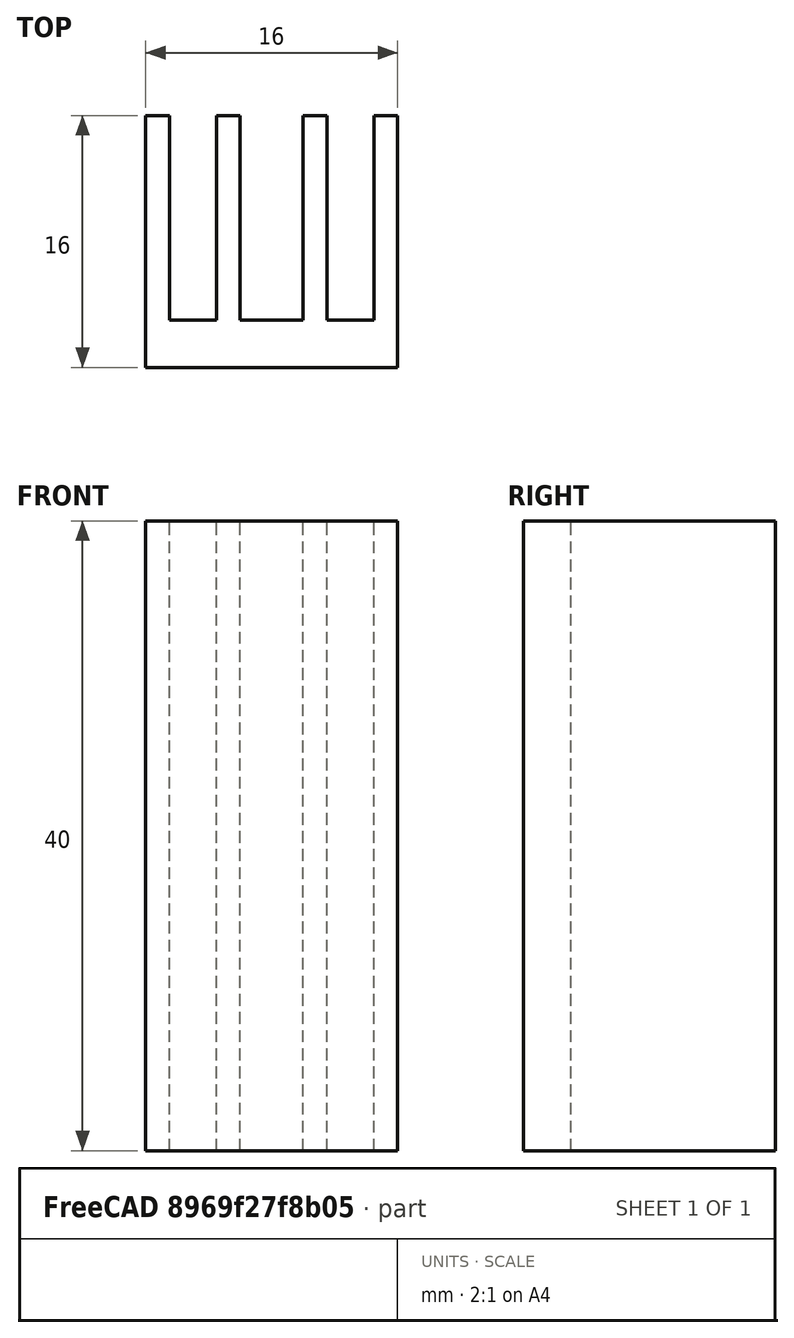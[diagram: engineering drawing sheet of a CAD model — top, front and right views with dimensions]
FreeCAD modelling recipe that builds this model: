
FCSTD DOCUMENT  (FreeCAD 0.21R33694 (Git))
Label: HEATSINK_16x40x16
License: All rights reserved
LicenseURL: https://en.wikipedia.org/wiki/All_rights_reserved
objects: Part::Part2DObjectPython×1, Part::Extrusion×1
note: 2 computed .brp shape members not serialized (recipe doc carries the construction recipe); baked Part::Feature solids carry a one-line shape summary decoded from their .brp

FEATURE [Part::Part2DObjectPython] Wire  # Draft 2D object (typed FeaturePython)
  Area = 0
  ChamferSize = 0
  Closed = false
  End = (3.62224,2.4175,-2.1e-15)
  FilletRadius = 0
  Length = 142
  MakeFace = true
  Placement = pos=(3.62224,2.4175,-2.1e-15) rot=(0,0,-1;0rad)
  Points = (17) [(0,0,0),(16,0,0),(16,16,0),(14.5,16,0),(14.5,3,0),(11.5,3,0),(11.5,16,0),(10,16,0),(10,3,0),(6,3,0),(6,16,0),(4.5,16,0),(4.5,3,0),(1.5,3,0),+3 more]
  Start = (3.62224,2.4175,-2.1e-15)
  Subdivisions = 0
FEATURE [Part::Extrusion] Extrude
  Base = -> Wire
  Dir = (0,9e-16,1)
  DirMode = 2
  FaceMakerClass = Part::FaceMakerBullseye
  LengthFwd = 40
  LengthRev = 0
  Solid = true
  Symmetric = false
